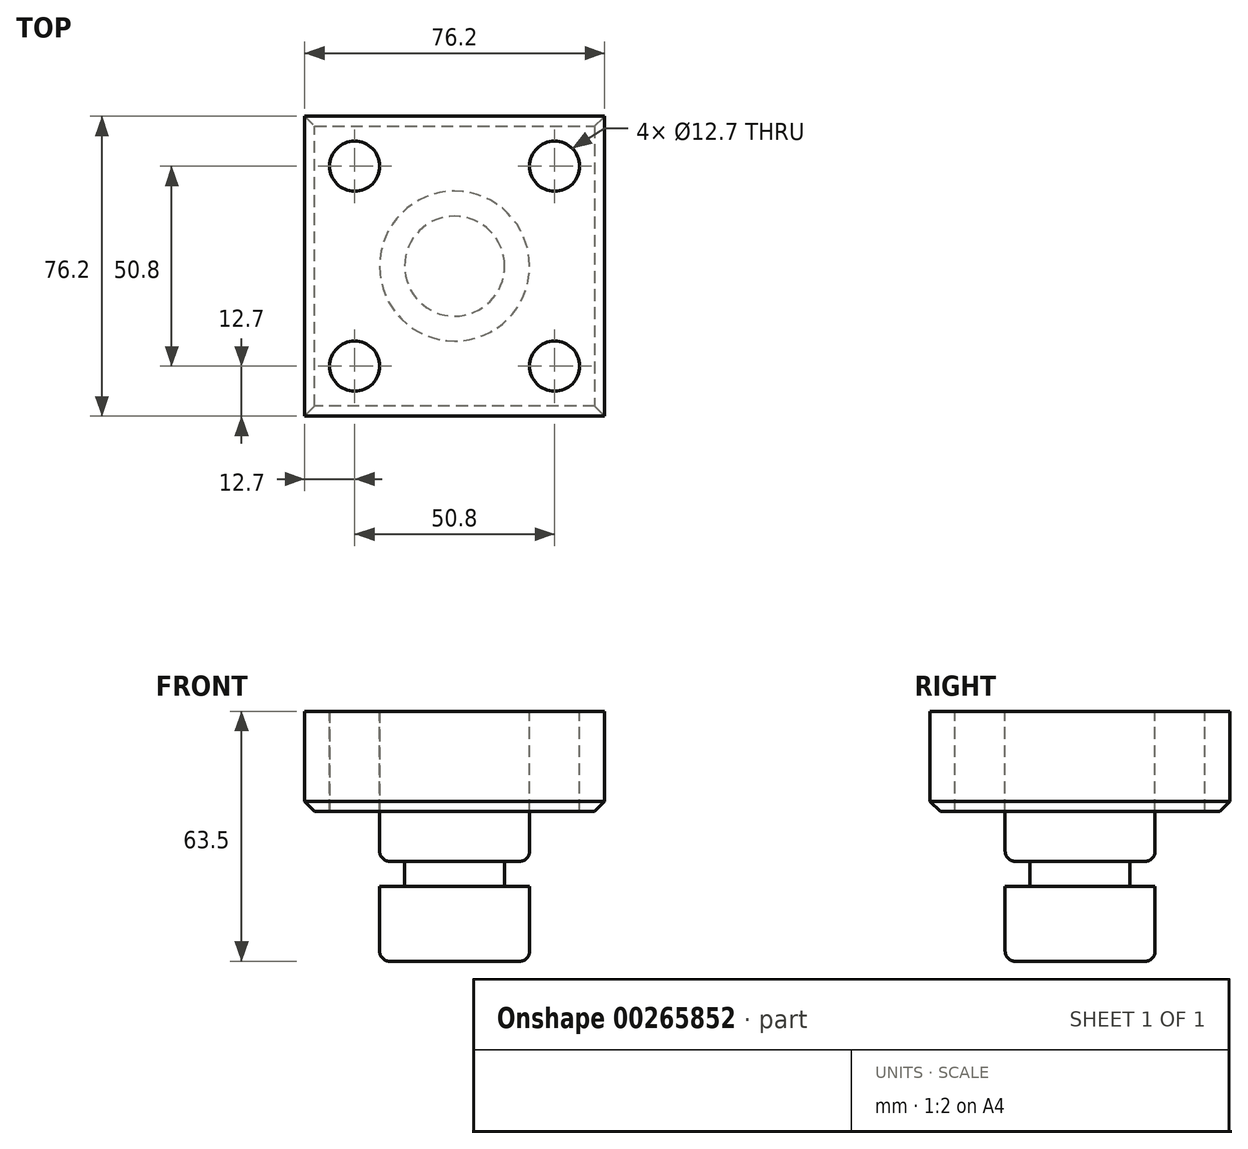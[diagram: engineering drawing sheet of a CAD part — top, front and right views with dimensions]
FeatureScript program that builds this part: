
annotation { "Feature Type Name" : "Feature", "Feature Type Description" : "" }
export const myFeature = defineFeature(function(context is Context, id is Id, definition is map)
    precondition{}
    {
        {
            var Q0;
            Q0=qCreatedBy(makeId("Top.planeOp"),FACE);
            var sketch = newSketch(context, id + "F0", { "sketchPlane" : qUnion([Q0])});
            skLineSegment(sketch, "E0.bottom", {"start": v(-38.1, 38.1) * mm, "end": v(38.1, 38.1) * mm});
            skLineSegment(sketch, "E0.top", {"start": v(-38.1, -38.1) * mm, "end": v(38.1, -38.1) * mm});
            skLineSegment(sketch, "E0.left", {"start": v(-38.1, 38.1) * mm, "end": v(-38.1, -38.1) * mm});
            skLineSegment(sketch, "E0.right", {"start": v(38.1, 38.1) * mm, "end": v(38.1, -38.1) * mm});
            skPoint(sketch, "E0.middle", {"position": v(0, 0) * mm});
            skSolve(sketch);
        }
        {
            var Q0;
            Q0=makeQuery(id+"F0.imprint","IMPRINT",FACE,{"disambiguationData":[TD([[makeQuery(id+"F0.imprint","IMPRINT",EDGE,{"derivedFrom":sQuery(id+"F0.wireOp",EDGE,"E0.bottom")}),-1.0]])]});
            extrude(context, id + "F1", {"entities" : qUnion([Q0]), "depth" : 25.4 * mm});
        }
        {
            var Q0;
            Q0=makeQuery(id+"F1.opExtrude","CAP_FACE",FACE,{"disambiguationData":[OSD([sQuery(id+"F0.wireOp",EDGE,"E0.bottom"),sQuery(id+"F0.wireOp",EDGE,"E0.top"),sQuery(id+"F0.wireOp",EDGE,"E0.left"),sQuery(id+"F0.wireOp",EDGE,"E0.right")])],"isStart":false});
            var sketch = newSketch(context, id + "F2", { "sketchPlane" : qUnion([Q0])});
            skCircle(sketch, "E1", {"center": v(25.4, 25.4) * mm, "radius": 6.35 * mm});
            skCircle(sketch, "E2", {"center": v(25.4, -25.4) * mm, "radius": 6.35 * mm});
            skCircle(sketch, "E3", {"center": v(-25.4, -25.4) * mm, "radius": 6.35 * mm});
            skSolve(sketch);
        }
        {
            var Q0;
            Q0 = qSketchRegion(id + "F2", true);
            extrude(context, id + "F3", {"entities" : qUnion([Q0]), "operationType" : NewBodyOperationType.REMOVE, "oppositeDirection" : true, "depth" : 25.4 * mm});
        }
        {
            var Q0;
            Q0=makeQuery(id+"F1.opExtrude","CAP_FACE",FACE,{"disambiguationData":[OSD([sQuery(id+"F0.wireOp",EDGE,"E0.bottom"),sQuery(id+"F0.wireOp",EDGE,"E0.top"),sQuery(id+"F0.wireOp",EDGE,"E0.left"),sQuery(id+"F0.wireOp",EDGE,"E0.right")])],"isStart":true});
            var sketch = newSketch(context, id + "F4", { "sketchPlane" : qUnion([Q0])});
            skCircle(sketch, "E4", {"center": v(-25.4, -25.4) * mm, "radius": 6.35 * mm});
            skSolve(sketch);
        }
        {
            var Q0;
            Q0 = qSketchRegion(id + "F4", true);
            var Q1;
            Q1=makeQuery(id+"F4.imprint","IMPRINT",FACE,{"disambiguationData":[TD([[makeQuery(id+"F4.imprint","IMPRINT",EDGE,{"derivedFrom":sQuery(id+"F4.wireOp",EDGE,"E4")}),1.0]])]});
            extrude(context, id + "F5", {"entities" : qUnion([Q0, Q1]), "operationType" : NewBodyOperationType.REMOVE, "oppositeDirection" : true, "depth" : 25.4 * mm});
        }
        {
            var Q0;
            Q0=qCreatedBy(makeId("Front.planeOp"),FACE);
            var sketch = newSketch(context, id + "F6", { "sketchPlane" : qUnion([Q0])});
            skLineSegment(sketch, "E5.bottom", {"start": v(19.05, -38.1) * mm, "end": v(0, -38.1) * mm});
            skLineSegment(sketch, "E5.top", {"start": v(19.05, 0) * mm, "end": v(0, 0) * mm});
            skLineSegment(sketch, "E5.left", {"start": v(19.05, -38.1) * mm, "end": v(19.05, 0) * mm});
            skLineSegment(sketch, "E5.right", {"start": v(0, -38.1) * mm, "end": v(0, 0) * mm});
            skSolve(sketch);
        }
        {
            var Q0;
            Q0=makeQuery(id+"F6.imprint","IMPRINT",FACE,{"disambiguationData":[TD([[makeQuery(id+"F6.imprint","IMPRINT",EDGE,{"derivedFrom":sQuery(id+"F6.wireOp",EDGE,"E5.bottom")}),-1.0]])]});
            var Q1;
            Q1=sQuery(id+"F6.wireOp",EDGE,"E5.right");
            revolve(context, id + "F7", {"operationType" : NewBodyOperationType.ADD, "entities" : qUnion([Q0]), "axis" : qUnion([Q1]), "revolveType" : RevolveType.FULL});
        }
        {
            var Q0;
            Q0=qCreatedBy(makeId("Right.planeOp"),FACE);
            var sketch = newSketch(context, id + "F8", { "sketchPlane" : qUnion([Q0])});
            skLineSegment(sketch, "E6.bottom", {"start": v(-20.97, -19.05) * mm, "end": v(-12.7, -19.05) * mm});
            skLineSegment(sketch, "E6.top", {"start": v(-20.97, -12.7) * mm, "end": v(-12.7, -12.7) * mm});
            skLineSegment(sketch, "E6.left", {"start": v(-20.97, -19.05) * mm, "end": v(-20.97, -12.7) * mm});
            skLineSegment(sketch, "E6.right", {"start": v(-12.7, -19.05) * mm, "end": v(-12.7, -12.7) * mm});
            skSolve(sketch);
        }
        {
            var Q0;
            Q0=makeQuery(id+"F8.imprint","IMPRINT",FACE,{"disambiguationData":[TD([[makeQuery(id+"F8.imprint","IMPRINT",EDGE,{"derivedFrom":sQuery(id+"F8.wireOp",EDGE,"E6.bottom")}),1.0]])]});
            var Q1;
            Q1=makeQuery(id+"F7.opRevolve","SWEPT_FACE",FACE,{"disambiguationData":[OSD([sQuery(id+"F6.wireOp",EDGE,"E5.left")])]});
            revolve(context, id + "F9", {"operationType" : NewBodyOperationType.REMOVE, "entities" : qUnion([Q0]), "axis" : qUnion([Q1]), "revolveType" : RevolveType.FULL, "oppositeDirection" : true});
        }
        {
            var Q0;
            Q0=makeQuery(id+"F1.opExtrude","CAP_EDGE",EDGE,{"disambiguationData":[OSD([sQuery(id+"F0.wireOp",EDGE,"E0.left")])],"isStart":true});
            var Q1;
            Q1=makeQuery(id+"F1.opExtrude","CAP_EDGE",EDGE,{"disambiguationData":[OSD([sQuery(id+"F0.wireOp",EDGE,"E0.bottom")])],"isStart":true});
            var Q2;
            Q2=makeQuery(id+"F1.opExtrude","CAP_EDGE",EDGE,{"disambiguationData":[OSD([sQuery(id+"F0.wireOp",EDGE,"E0.right")])],"isStart":true});
            var Q3;
            Q3=makeQuery(id+"F1.opExtrude","CAP_EDGE",EDGE,{"disambiguationData":[OSD([sQuery(id+"F0.wireOp",EDGE,"E0.top")])],"isStart":true});
            chamfer(context, id + "F10", {"entities" : qUnion([Q0, Q1, Q2, Q3]), "width" : 2.54 * mm, "tangentPropagation" : true});
        }
        {
            var Q0;
            Q0=makeQuery(id+"F9.boolean.opBoolean","INTERSECT",EDGE,{"derivedFrom":[makeQuery(id+"F7.opRevolve","SWEPT_FACE",FACE,{"disambiguationData":[OSD([sQuery(id+"F6.wireOp",EDGE,"E5.left")])]}),makeQuery(id+"F9.opRevolve","SWEPT_FACE",FACE,{"disambiguationData":[OSD([sQuery(id+"F8.wireOp",EDGE,"E6.top")])]})]});
            var Q1;
            Q1=makeQuery(id+"F7.opRevolve","SWEPT_EDGE",EDGE,{"disambiguationData":[OSD([sQuery(id+"F6.wireOp",EDGE,"E5.top"),sQuery(id+"F6.wireOp",EDGE,"E5.left")])]});
            var Q2;
            Q2=makeQuery(id+"F7.opRevolve","SWEPT_EDGE",EDGE,{"disambiguationData":[OSD([sQuery(id+"F6.wireOp",EDGE,"E5.bottom"),sQuery(id+"F6.wireOp",EDGE,"E5.left")])]});
            fillet(context, id + "F11", {"entities" : qUnion([Q0, Q1, Q2]), "radius" : 2.54 * mm, "tangentPropagation" : true, "allowEdgeOverflow" : false});
        }
    });
